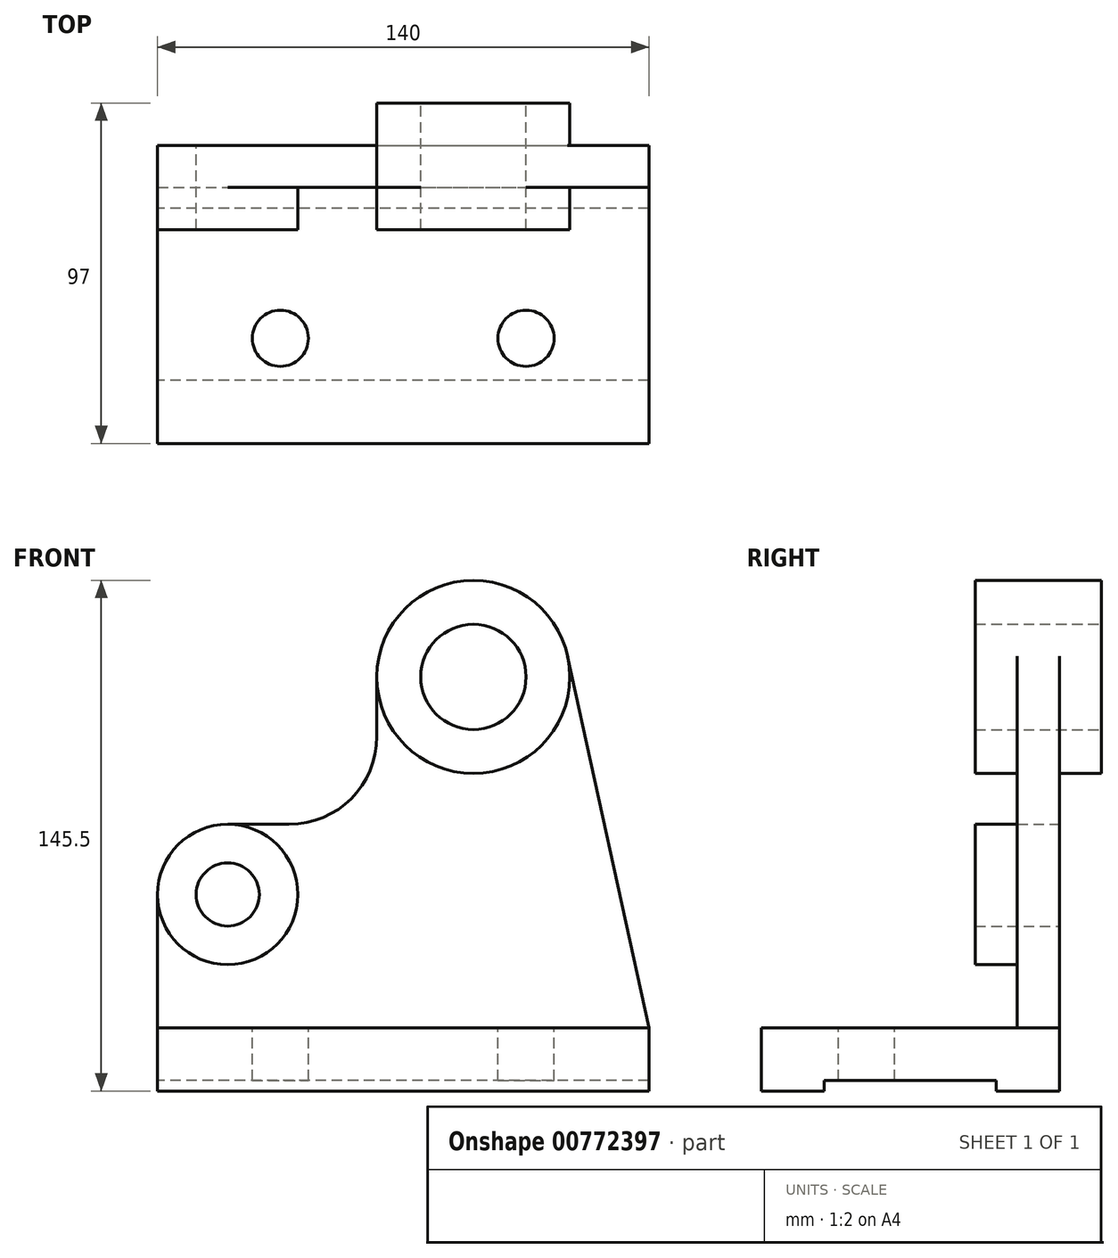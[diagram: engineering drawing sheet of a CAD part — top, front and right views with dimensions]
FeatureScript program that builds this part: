
annotation { "Feature Type Name" : "Feature", "Feature Type Description" : "" }
export const myFeature = defineFeature(function(context is Context, id is Id, definition is map)
    precondition{}
    {
        {
            var Q0;
            Q0=qCreatedBy(makeId("Front.planeOp"),FACE);
            var sketch = newSketch(context, id + "F0", { "sketchPlane" : qUnion([Q0])});
            skCircle(sketch, "E0", {"center": v(20, 56) * mm, "radius": 9 * mm});
            skCircle(sketch, "E1", {"center": v(90, 118) * mm, "radius": 15 * mm});
            skCircle(sketch, "E2", {"center": v(20, 56) * mm, "radius": 20 * mm});
            skCircle(sketch, "E3", {"center": v(90, 118) * mm, "radius": 27.5 * mm});
            skLineSegment(sketch, "E4", {"start": v(0, 0) * mm, "end": v(245.49, 0) * mm, "construction": true});
            skLineSegment(sketch, "E5", {"start": v(0, 56) * mm, "end": v(0, 0) * mm});
            skLineSegment(sketch, "E6", {"start": v(20, 76) * mm, "end": v(62.5, 76) * mm});
            skLineSegment(sketch, "E7", {"start": v(62.5, 76) * mm, "end": v(62.5, 118) * mm});
            skLineSegment(sketch, "E8", {"start": v(0, 0) * mm, "end": v(140, 0) * mm});
            skLineSegment(sketch, "E9", {"start": v(140, 0) * mm, "end": v(140, 18) * mm});
            skLineSegment(sketch, "E10", {"start": v(140, 18) * mm, "end": v(116.87, 123.87) * mm});
            skLineSegment(sketch, "E11", {"start": v(90, 118) * mm, "end": v(90, 28) * mm, "construction": true});
            skLineSegment(sketch, "E12", {"start": v(140, 18) * mm, "end": v(0, 18) * mm});
            skSolve(sketch);
        }
        {
            var Q0;
            {var subQ7=sQuery(id+"F0.wireOp",EDGE,"E6");Q0=makeQuery(id+"F0.imprint","IMPRINT",FACE,{"disambiguationData":[TD([[makeQuery(id+"F0.imprint","IMPRINT",EDGE,{"derivedFrom":subQ7}),-1.0]])]});}
            var Q1;
            {var subQ0=sQuery(id+"F0.wireOp",EDGE,"E8");Q1=makeQuery(id+"F0.imprint","IMPRINT",FACE,{"disambiguationData":[TD([[makeQuery(id+"F0.imprint","IMPRINT",EDGE,{"derivedFrom":subQ0}),1.0]])]});}
            extrude(context, id + "F1", {"entities" : qUnion([Q0, Q1]), "depth" : 12 * mm, "offsetDistance" : 25 * mm});
        }
        {
            var Q0;
            Q0=makeQuery(id+"F1.opExtrude","SWEPT_EDGE",EDGE,{"disambiguationData":[OSD([sQuery(id+"F0.wireOp",EDGE,"E6"),sQuery(id+"F0.wireOp",EDGE,"E7")])]});
            fillet(context, id + "F2", {"entities" : qUnion([Q0]), "radius" : 25 * mm, "tangentPropagation" : true, "allowEdgeOverflow" : false});
        }
        {
            var Q0;
            Q0=makeQuery(id+"F0.imprint","IMPRINT",FACE,{"disambiguationData":[TD([[makeQuery(id+"F0.imprint","IMPRINT",EDGE,{"derivedFrom":sQuery(id+"F0.wireOp",EDGE,"E0")}),-1.0]])]});
            extrude(context, id + "F3", {"entities" : qUnion([Q0]), "operationType" : NewBodyOperationType.ADD, "depth" : 24 * mm, "offsetDistance" : 25 * mm});
        }
        {
            var Q0;
            Q0=makeQuery(id+"F0.imprint","IMPRINT",FACE,{"disambiguationData":[TD([[makeQuery(id+"F0.imprint","IMPRINT",EDGE,{"derivedFrom":sQuery(id+"F0.wireOp",EDGE,"E1")}),-1.0]])]});
            extrude(context, id + "F4", {"entities" : qUnion([Q0]), "operationType" : NewBodyOperationType.ADD, "depth" : 24 * mm, "offsetDistance" : 25 * mm});
        }
        {
            var Q0;
            Q0=makeQuery(id+"F0.imprint","IMPRINT",FACE,{"disambiguationData":[TD([[makeQuery(id+"F0.imprint","IMPRINT",EDGE,{"derivedFrom":sQuery(id+"F0.wireOp",EDGE,"E1")}),-1.0]])]});
            extrude(context, id + "F5", {"entities" : qUnion([Q0]), "operationType" : NewBodyOperationType.ADD, "oppositeDirection" : true, "depth" : 12 * mm, "offsetDistance" : 25 * mm});
        }
        {
            var Q0;
            {var subQ0=sQuery(id+"F0.wireOp",EDGE,"E8");Q0=makeQuery(id+"F0.imprint","IMPRINT",FACE,{"disambiguationData":[TD([[makeQuery(id+"F0.imprint","IMPRINT",EDGE,{"derivedFrom":subQ0}),1.0]])]});}
            extrude(context, id + "F6", {"entities" : qUnion([Q0]), "operationType" : NewBodyOperationType.ADD, "depth" : 85 * mm, "offsetDistance" : 25 * mm});
        }
        {
            var Q0;
            {var subQ0=sQuery(id+"F0.wireOp",EDGE,"E5");Q0=makeQuery(id+"F6.boolean.opBoolean","MERGE",FACE,{"derivedFrom":[makeQuery(id+"F1.opExtrude","SWEPT_FACE",FACE,{"disambiguationData":[OSD([subQ0])]}),makeQuery(id+"F6.opExtrude","SWEPT_FACE",FACE,{"disambiguationData":[OSD([subQ0])]})]});}
            var sketch = newSketch(context, id + "F7", { "sketchPlane" : qUnion([Q0])});
            skLineSegment(sketch, "E13.bottom", {"start": v(18, 0) * mm, "end": v(67, 0) * mm});
            skLineSegment(sketch, "E13.top", {"start": v(18, 3) * mm, "end": v(67, 3) * mm});
            skLineSegment(sketch, "E13.left", {"start": v(18, 0) * mm, "end": v(18, 3) * mm});
            skLineSegment(sketch, "E13.right", {"start": v(67, 0) * mm, "end": v(67, 3) * mm});
            skSolve(sketch);
        }
        {
            var Q0;
            Q0=qSketchRegion(id+"F7",true);
            extrude(context, id + "F8", {"entities" : qUnion([Q0]), "operationType" : NewBodyOperationType.REMOVE, "endBound" : BoundingType.THROUGH_ALL, "oppositeDirection" : true, "depth" : 25 * mm, "offsetDistance" : 25 * mm});
        }
        {
            var Q0;
            Q0=makeQuery(id+"F6.opExtrude","SWEPT_FACE",FACE,{"disambiguationData":[OSD([sQuery(id+"F0.wireOp",EDGE,"E12")])]});
            var sketch = newSketch(context, id + "F9", { "sketchPlane" : qUnion([Q0])});
            skLineSegment(sketch, "E14", {"start": v(0, -55) * mm, "end": v(140, -55) * mm, "construction": true});
            skPoint(sketch, "E14.endSnap0", {"position": v(140, -48.5) * mm});
            skCircle(sketch, "E15", {"center": v(35, -55) * mm, "radius": 8 * mm});
            skCircle(sketch, "E16", {"center": v(105, -55) * mm, "radius": 8 * mm});
            skSolve(sketch);
        }
        {
            var Q0;
            Q0=qSketchRegion(id+"F9",true);
            extrude(context, id + "F10", {"entities" : qUnion([Q0]), "operationType" : NewBodyOperationType.REMOVE, "endBound" : BoundingType.THROUGH_ALL, "oppositeDirection" : true, "depth" : 25 * mm, "offsetDistance" : 25 * mm});
        }
    });
